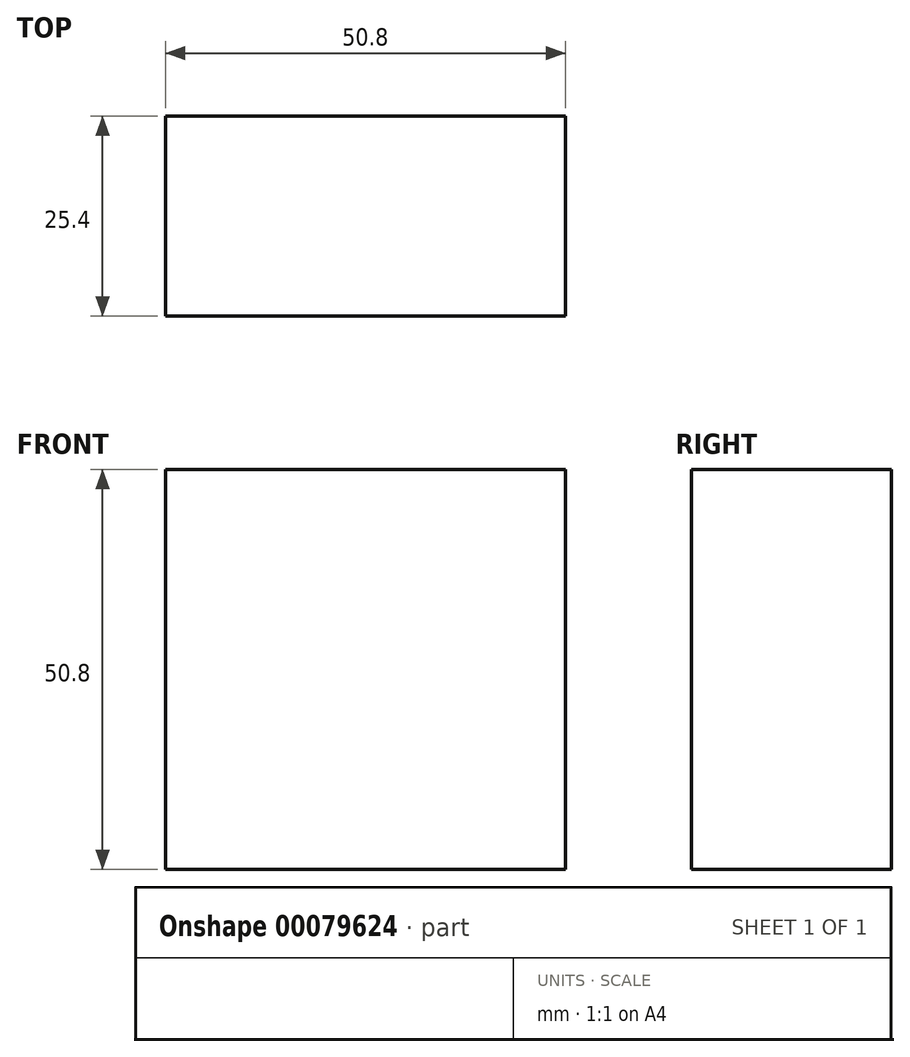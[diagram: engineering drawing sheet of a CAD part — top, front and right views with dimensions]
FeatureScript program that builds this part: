
annotation { "Feature Type Name" : "Feature", "Feature Type Description" : "" }
export const myFeature = defineFeature(function(context is Context, id is Id, definition is map)
    precondition{}
    {
        {
            var Q0;
            Q0=qCreatedBy(makeId("Front.planeOp"),FACE);
            var sketch = newSketch(context, id + "F0", { "sketchPlane" : qUnion([Q0])});
            skLineSegment(sketch, "E0", {"start": v(0, 0) * mm, "end": v(0, 50.8) * mm});
            skLineSegment(sketch, "E1", {"start": v(0, 50.8) * mm, "end": v(50.8, 50.8) * mm});
            skLineSegment(sketch, "E2", {"start": v(50.8, 50.8) * mm, "end": v(50.8, 0) * mm});
            skLineSegment(sketch, "E3", {"start": v(50.8, 0) * mm, "end": v(0, 0) * mm});
            skSolve(sketch);
        }
        {
            var Q0;
            Q0 = qSketchRegion(id + "F0", true);
            extrude(context, id + "F1", {"entities" : qUnion([Q0]), "depth" : 25.4 * mm});
        }
    });
